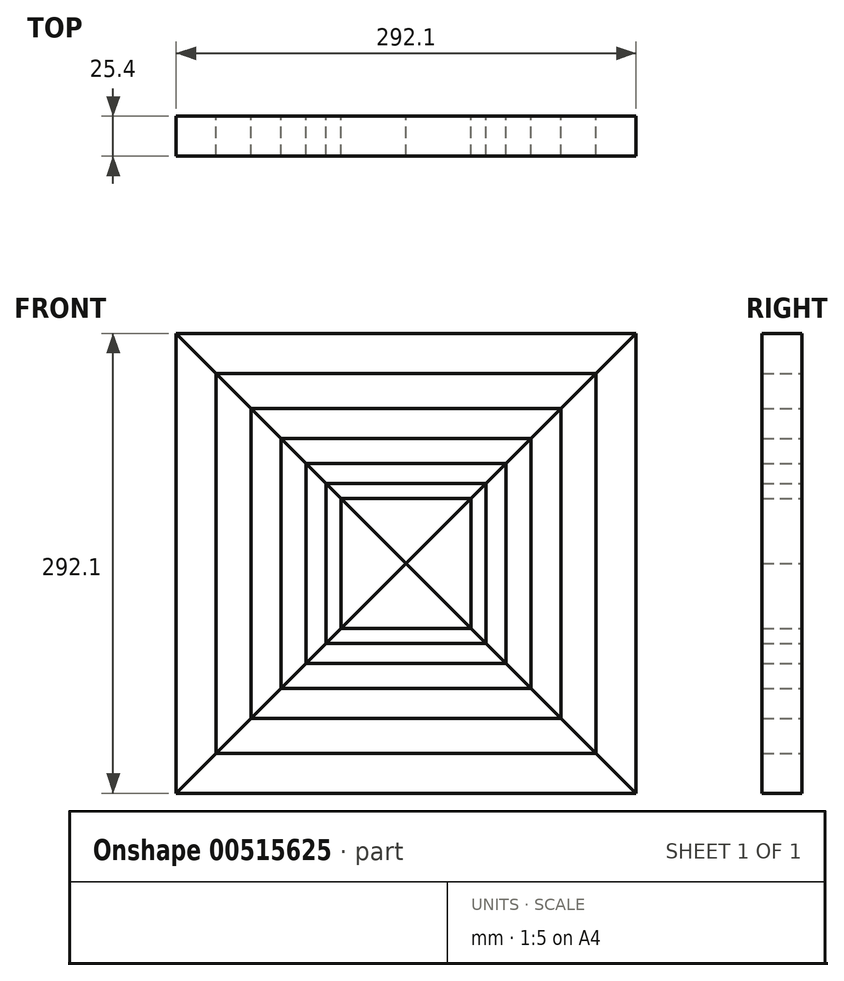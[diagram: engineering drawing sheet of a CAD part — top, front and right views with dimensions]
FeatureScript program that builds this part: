
annotation { "Feature Type Name" : "Feature", "Feature Type Description" : "" }
export const myFeature = defineFeature(function(context is Context, id is Id, definition is map)
    precondition{}
    {
        {
            var Q0;
            Q0=qCreatedBy(makeId("Front.planeOp"),FACE);
            var sketch = newSketch(context, id + "F0", { "sketchPlane" : qUnion([Q0])});
            skLineSegment(sketch, "E0.bottom", {"start": v(146.05, 146.05) * mm, "end": v(-146.05, 146.05) * mm});
            skLineSegment(sketch, "E0.top", {"start": v(146.05, -146.05) * mm, "end": v(-146.05, -146.05) * mm});
            skLineSegment(sketch, "E0.left", {"start": v(146.05, 146.05) * mm, "end": v(146.05, -146.05) * mm});
            skLineSegment(sketch, "E0.right", {"start": v(-146.05, 146.05) * mm, "end": v(-146.05, -146.05) * mm});
            skPoint(sketch, "E0.middle", {"position": v(0, 0) * mm});
            skLineSegment(sketch, "E1", {"start": v(-146.05, 146.05) * mm, "end": v(146.05, -146.05) * mm});
            skLineSegment(sketch, "E2", {"start": v(146.05, 146.05) * mm, "end": v(-146.05, -146.05) * mm});
            skLineSegment(sketch, "E3.0", {"start": v(120.65, 120.65) * mm, "end": v(-120.65, 120.65) * mm});
            skLineSegment(sketch, "E3.1", {"start": v(120.65, 120.65) * mm, "end": v(120.65, -120.65) * mm});
            skLineSegment(sketch, "E3.2", {"start": v(120.65, -120.65) * mm, "end": v(-120.65, -120.65) * mm});
            skLineSegment(sketch, "E3.3", {"start": v(-120.65, 120.65) * mm, "end": v(-120.65, -120.65) * mm});
            skLineSegment(sketch, "E4.0", {"start": v(98.43, 98.43) * mm, "end": v(-98.42, 98.43) * mm});
            skLineSegment(sketch, "E4.1", {"start": v(98.43, 98.43) * mm, "end": v(98.43, -98.43) * mm});
            skLineSegment(sketch, "E4.2", {"start": v(98.43, -98.43) * mm, "end": v(-98.43, -98.43) * mm});
            skLineSegment(sketch, "E4.3", {"start": v(-98.42, 98.43) * mm, "end": v(-98.43, -98.43) * mm});
            skLineSegment(sketch, "E5.0", {"start": v(79.38, 79.38) * mm, "end": v(-79.38, 79.38) * mm});
            skLineSegment(sketch, "E5.1", {"start": v(79.38, 79.38) * mm, "end": v(79.38, -79.38) * mm});
            skLineSegment(sketch, "E5.2", {"start": v(79.38, -79.38) * mm, "end": v(-79.38, -79.38) * mm});
            skLineSegment(sketch, "E5.3", {"start": v(-79.38, 79.38) * mm, "end": v(-79.38, -79.38) * mm});
            skLineSegment(sketch, "E6.0", {"start": v(63.5, 63.5) * mm, "end": v(-63.5, 63.5) * mm});
            skLineSegment(sketch, "E6.1", {"start": v(63.5, 63.5) * mm, "end": v(63.5, -63.5) * mm});
            skLineSegment(sketch, "E6.2", {"start": v(63.5, -63.5) * mm, "end": v(-63.5, -63.5) * mm});
            skLineSegment(sketch, "E6.3", {"start": v(-63.5, 63.5) * mm, "end": v(-63.5, -63.5) * mm});
            skLineSegment(sketch, "E7.0", {"start": v(50.8, 50.8) * mm, "end": v(-50.8, 50.8) * mm});
            skLineSegment(sketch, "E7.1", {"start": v(50.8, 50.8) * mm, "end": v(50.8, -50.8) * mm});
            skLineSegment(sketch, "E7.2", {"start": v(50.8, -50.8) * mm, "end": v(-50.8, -50.8) * mm});
            skLineSegment(sketch, "E7.3", {"start": v(-50.8, 50.8) * mm, "end": v(-50.8, -50.8) * mm});
            skLineSegment(sketch, "E8.0", {"start": v(41.28, 41.28) * mm, "end": v(-41.28, 41.28) * mm});
            skLineSegment(sketch, "E8.1", {"start": v(41.28, 41.28) * mm, "end": v(41.28, -41.28) * mm});
            skLineSegment(sketch, "E8.2", {"start": v(41.28, -41.28) * mm, "end": v(-41.28, -41.28) * mm});
            skLineSegment(sketch, "E8.3", {"start": v(-41.28, 41.28) * mm, "end": v(-41.28, -41.28) * mm});
            skSolve(sketch);
        }
        {
            var Q0;
            {var subQ0=sQuery(id+"F0.wireOp",EDGE,"E0.bottom");Q0=makeQuery(id+"F0.imprint","IMPRINT",FACE,{"disambiguationData":[TD([[makeQuery(id+"F0.imprint","IMPRINT",EDGE,{"derivedFrom":subQ0}),1.0]])]});}
            var Q1;
            {var subQ0=sQuery(id+"F0.wireOp",EDGE,"E4.0");Q1=makeQuery(id+"F0.imprint","IMPRINT",FACE,{"disambiguationData":[TD([[makeQuery(id+"F0.imprint","IMPRINT",EDGE,{"derivedFrom":subQ0}),1.0]])]});}
            var Q2;
            {var subQ0=sQuery(id+"F0.wireOp",EDGE,"E6.0");Q2=makeQuery(id+"F0.imprint","IMPRINT",FACE,{"disambiguationData":[TD([[makeQuery(id+"F0.imprint","IMPRINT",EDGE,{"derivedFrom":subQ0}),1.0]])]});}
            var Q3;
            {var subQ0=sQuery(id+"F0.wireOp",EDGE,"E8.0");Q3=makeQuery(id+"F0.imprint","IMPRINT",FACE,{"disambiguationData":[TD([[makeQuery(id+"F0.imprint","IMPRINT",EDGE,{"derivedFrom":subQ0}),1.0]])]});}
            var Q4;
            {var subQ0=sQuery(id+"F0.wireOp",EDGE,"E6.2");Q4=makeQuery(id+"F0.imprint","IMPRINT",FACE,{"disambiguationData":[TD([[makeQuery(id+"F0.imprint","IMPRINT",EDGE,{"derivedFrom":subQ0}),-1.0]])]});}
            var Q5;
            {var subQ0=sQuery(id+"F0.wireOp",EDGE,"E8.2");Q5=makeQuery(id+"F0.imprint","IMPRINT",FACE,{"disambiguationData":[TD([[makeQuery(id+"F0.imprint","IMPRINT",EDGE,{"derivedFrom":subQ0}),-1.0]])]});}
            var Q6;
            {var subQ0=sQuery(id+"F0.wireOp",EDGE,"E4.2");Q6=makeQuery(id+"F0.imprint","IMPRINT",FACE,{"disambiguationData":[TD([[makeQuery(id+"F0.imprint","IMPRINT",EDGE,{"derivedFrom":subQ0}),-1.0]])]});}
            var Q7;
            {var subQ0=sQuery(id+"F0.wireOp",EDGE,"E0.top");Q7=makeQuery(id+"F0.imprint","IMPRINT",FACE,{"disambiguationData":[TD([[makeQuery(id+"F0.imprint","IMPRINT",EDGE,{"derivedFrom":subQ0}),-1.0]])]});}
            var Q8;
            {var subQ0=sQuery(id+"F0.wireOp",EDGE,"E3.1");Q8=makeQuery(id+"F0.imprint","IMPRINT",FACE,{"disambiguationData":[TD([[makeQuery(id+"F0.imprint","IMPRINT",EDGE,{"derivedFrom":subQ0}),-1.0]])]});}
            var Q9;
            {var subQ0=sQuery(id+"F0.wireOp",EDGE,"E5.1");Q9=makeQuery(id+"F0.imprint","IMPRINT",FACE,{"disambiguationData":[TD([[makeQuery(id+"F0.imprint","IMPRINT",EDGE,{"derivedFrom":subQ0}),-1.0]])]});}
            var Q10;
            {var subQ0=sQuery(id+"F0.wireOp",EDGE,"E5.3");Q10=makeQuery(id+"F0.imprint","IMPRINT",FACE,{"disambiguationData":[TD([[makeQuery(id+"F0.imprint","IMPRINT",EDGE,{"derivedFrom":subQ0}),1.0]])]});}
            var Q11;
            {var subQ0=sQuery(id+"F0.wireOp",EDGE,"E3.3");Q11=makeQuery(id+"F0.imprint","IMPRINT",FACE,{"disambiguationData":[TD([[makeQuery(id+"F0.imprint","IMPRINT",EDGE,{"derivedFrom":subQ0}),1.0]])]});}
            var Q12;
            {var subQ0=sQuery(id+"F0.wireOp",EDGE,"E7.1");Q12=makeQuery(id+"F0.imprint","IMPRINT",FACE,{"disambiguationData":[TD([[makeQuery(id+"F0.imprint","IMPRINT",EDGE,{"derivedFrom":subQ0}),-1.0]])]});}
            var Q13;
            {var subQ0=sQuery(id+"F0.wireOp",EDGE,"E7.3");Q13=makeQuery(id+"F0.imprint","IMPRINT",FACE,{"disambiguationData":[TD([[makeQuery(id+"F0.imprint","IMPRINT",EDGE,{"derivedFrom":subQ0}),1.0]])]});}
            extrude(context, id + "F1", {"entities" : qUnion([Q0, Q1, Q2, Q3, Q4, Q5, Q6, Q7, Q8, Q9, Q10, Q11, Q12, Q13]), "depth" : 25.4 * mm, "offsetDistance" : 25.4 * mm});
        }
        {
            var Q0;
            {var subQ0=sQuery(id+"F0.wireOp",EDGE,"E3.0");Q0=makeQuery(id+"F0.imprint","IMPRINT",FACE,{"disambiguationData":[TD([[makeQuery(id+"F0.imprint","IMPRINT",EDGE,{"derivedFrom":subQ0}),1.0]])]});}
            var Q1;
            {var subQ0=sQuery(id+"F0.wireOp",EDGE,"E0.right");Q1=makeQuery(id+"F0.imprint","IMPRINT",FACE,{"disambiguationData":[TD([[makeQuery(id+"F0.imprint","IMPRINT",EDGE,{"derivedFrom":subQ0}),1.0]])]});}
            var Q2;
            {var subQ0=sQuery(id+"F0.wireOp",EDGE,"E0.left");Q2=makeQuery(id+"F0.imprint","IMPRINT",FACE,{"disambiguationData":[TD([[makeQuery(id+"F0.imprint","IMPRINT",EDGE,{"derivedFrom":subQ0}),-1.0]])]});}
            var Q3;
            {var subQ0=sQuery(id+"F0.wireOp",EDGE,"E4.1");Q3=makeQuery(id+"F0.imprint","IMPRINT",FACE,{"disambiguationData":[TD([[makeQuery(id+"F0.imprint","IMPRINT",EDGE,{"derivedFrom":subQ0}),-1.0]])]});}
            var Q4;
            {var subQ0=sQuery(id+"F0.wireOp",EDGE,"E5.0");Q4=makeQuery(id+"F0.imprint","IMPRINT",FACE,{"disambiguationData":[TD([[makeQuery(id+"F0.imprint","IMPRINT",EDGE,{"derivedFrom":subQ0}),1.0]])]});}
            var Q5;
            {var subQ0=sQuery(id+"F0.wireOp",EDGE,"E4.3");Q5=makeQuery(id+"F0.imprint","IMPRINT",FACE,{"disambiguationData":[TD([[makeQuery(id+"F0.imprint","IMPRINT",EDGE,{"derivedFrom":subQ0}),1.0]])]});}
            var Q6;
            {var subQ0=sQuery(id+"F0.wireOp",EDGE,"E6.3");Q6=makeQuery(id+"F0.imprint","IMPRINT",FACE,{"disambiguationData":[TD([[makeQuery(id+"F0.imprint","IMPRINT",EDGE,{"derivedFrom":subQ0}),1.0]])]});}
            var Q7;
            {var subQ0=sQuery(id+"F0.wireOp",EDGE,"E7.0");Q7=makeQuery(id+"F0.imprint","IMPRINT",FACE,{"disambiguationData":[TD([[makeQuery(id+"F0.imprint","IMPRINT",EDGE,{"derivedFrom":subQ0}),1.0]])]});}
            var Q8;
            {var subQ0=sQuery(id+"F0.wireOp",EDGE,"E6.1");Q8=makeQuery(id+"F0.imprint","IMPRINT",FACE,{"disambiguationData":[TD([[makeQuery(id+"F0.imprint","IMPRINT",EDGE,{"derivedFrom":subQ0}),-1.0]])]});}
            var Q9;
            {var subQ0=sQuery(id+"F0.wireOp",EDGE,"E8.1");Q9=makeQuery(id+"F0.imprint","IMPRINT",FACE,{"disambiguationData":[TD([[makeQuery(id+"F0.imprint","IMPRINT",EDGE,{"derivedFrom":subQ0}),-1.0]])]});}
            var Q10;
            {var subQ0=sQuery(id+"F0.wireOp",EDGE,"E8.3");Q10=makeQuery(id+"F0.imprint","IMPRINT",FACE,{"disambiguationData":[TD([[makeQuery(id+"F0.imprint","IMPRINT",EDGE,{"derivedFrom":subQ0}),1.0]])]});}
            var Q11;
            {var subQ0=sQuery(id+"F0.wireOp",EDGE,"E7.2");Q11=makeQuery(id+"F0.imprint","IMPRINT",FACE,{"disambiguationData":[TD([[makeQuery(id+"F0.imprint","IMPRINT",EDGE,{"derivedFrom":subQ0}),-1.0]])]});}
            var Q12;
            {var subQ0=sQuery(id+"F0.wireOp",EDGE,"E5.2");Q12=makeQuery(id+"F0.imprint","IMPRINT",FACE,{"disambiguationData":[TD([[makeQuery(id+"F0.imprint","IMPRINT",EDGE,{"derivedFrom":subQ0}),-1.0]])]});}
            var Q13;
            {var subQ0=sQuery(id+"F0.wireOp",EDGE,"E3.2");Q13=makeQuery(id+"F0.imprint","IMPRINT",FACE,{"disambiguationData":[TD([[makeQuery(id+"F0.imprint","IMPRINT",EDGE,{"derivedFrom":subQ0}),-1.0]])]});}
            extrude(context, id + "F2", {"entities" : qUnion([Q0, Q1, Q2, Q3, Q4, Q5, Q6, Q7, Q8, Q9, Q10, Q11, Q12, Q13]), "depth" : 25.4 * mm, "offsetDistance" : 25.4 * mm});
        }
    });
